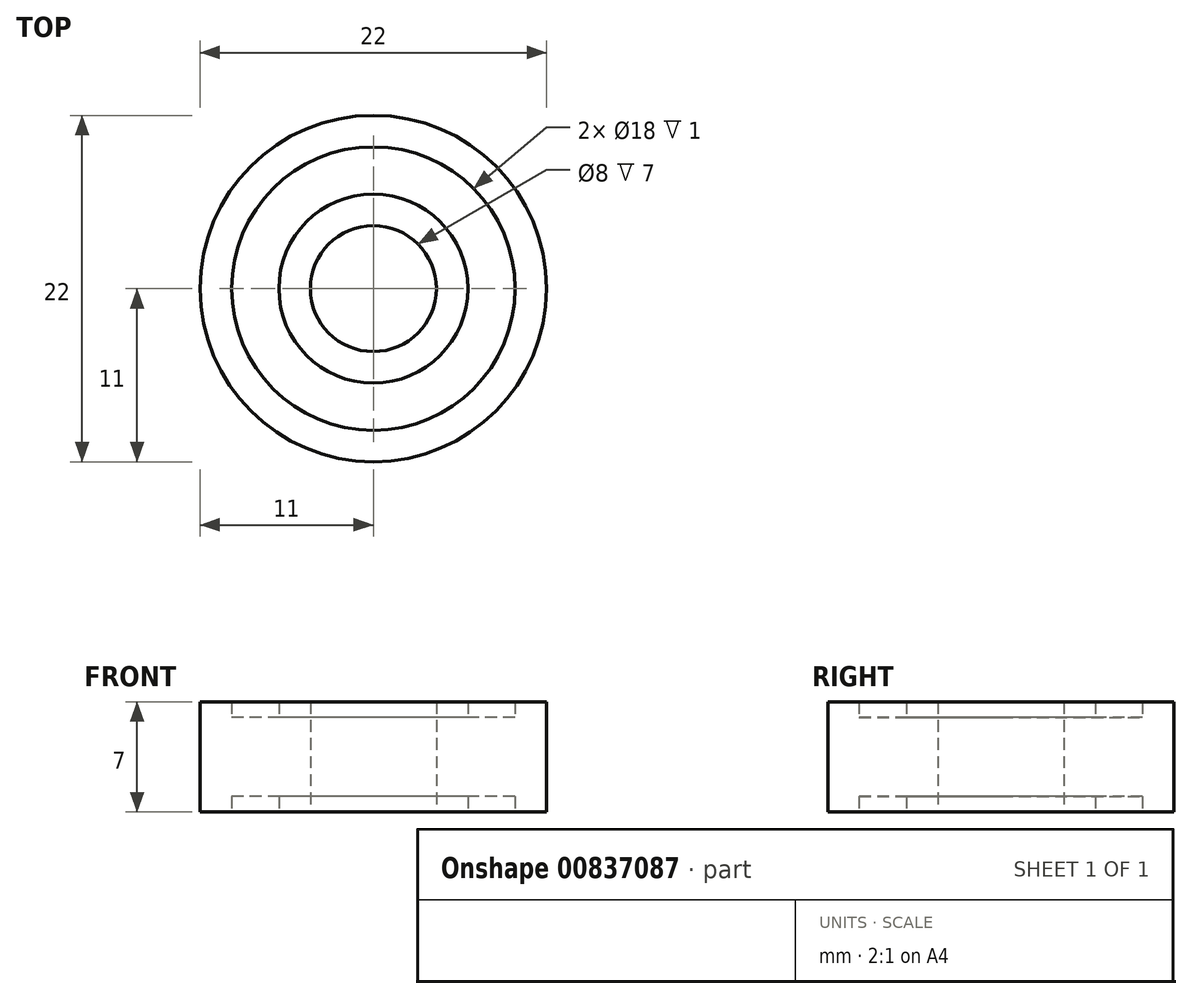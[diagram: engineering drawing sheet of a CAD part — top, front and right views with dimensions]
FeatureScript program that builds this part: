
annotation { "Feature Type Name" : "Feature", "Feature Type Description" : "" }
export const myFeature = defineFeature(function(context is Context, id is Id, definition is map)
    precondition{}
    {
        {
            var Q0;
            Q0=qCreatedBy(makeId("Top.planeOp"),FACE);
            var sketch = newSketch(context, id + "F0", { "sketchPlane" : qUnion([Q0])});
            skCircle(sketch, "E0", {"center": v(0, 0) * mm, "radius": 4 * mm});
            skCircle(sketch, "E1", {"center": v(0, 0) * mm, "radius": 11 * mm});
            skSolve(sketch);
        }
        {
            var Q0;
            Q0=makeQuery(id+"F0.imprint","IMPRINT",FACE,{"disambiguationData":[TD([[makeQuery(id+"F0.imprint","IMPRINT",EDGE,{"derivedFrom":sQuery(id+"F0.wireOp",EDGE,"E0")}),-1.0]])]});
            extrude(context, id + "F1", {"entities" : qUnion([Q0]), "depth" : 7 * mm, "offsetDistance" : 25 * mm});
        }
        {
            var Q0;
            Q0=makeQuery(id+"F1.opExtrude","CAP_FACE",FACE,{"disambiguationData":[OSD([sQuery(id+"F0.wireOp",EDGE,"E0"),sQuery(id+"F0.wireOp",EDGE,"E1")])],"isStart":false});
            shell(context, id + "F2", {"entities" : qUnion([Q0]), "thickness" : 2 * mm});
        }
        {
            var Q0;
            {var subQ0=sQuery(id+"F0.wireOp",EDGE,"E1");var subQ1=sQuery(id+"F0.wireOp",EDGE,"E0");Q0=makeQuery(id+"F2.opShell","OFFSET_FACE",FACE,{"disambiguationData":[OSD([subQ1,subQ0]),TDD([makeQuery(id+"F1.opExtrude","CAP_FACE",FACE,{"disambiguationData":[OSD([subQ1,subQ0])],"isStart":true})])]});}
            extrude(context, id + "F3", {"entities" : qUnion([Q0]), "operationType" : NewBodyOperationType.ADD, "depth" : 4 * mm, "offsetDistance" : 25 * mm});
        }
        {
            var Q0;
            Q0=makeQuery(id+"F1.opExtrude","CAP_FACE",FACE,{"disambiguationData":[OSD([sQuery(id+"F0.wireOp",EDGE,"E0"),sQuery(id+"F0.wireOp",EDGE,"E1")])],"isStart":true});
            shell(context, id + "F4", {"entities" : qUnion([Q0]), "thickness" : 2 * mm});
        }
        {
            var Q0;
            {var subQ0=sQuery(id+"F0.wireOp",EDGE,"E1");var subQ1=sQuery(id+"F0.wireOp",EDGE,"E0");Q0=makeQuery(id+"F4.opShell","OFFSET_FACE",FACE,{"disambiguationData":[OSD([subQ1,subQ0]),TDD([makeQuery(id+"F3.opExtrude","CAP_FACE",FACE,{"disambiguationData":[OSD([subQ1,subQ0])],"isStart":false})])]});}
            extrude(context, id + "F5", {"entities" : qUnion([Q0]), "operationType" : NewBodyOperationType.ADD, "depth" : 3 * mm, "offsetDistance" : 25 * mm});
        }
    });
